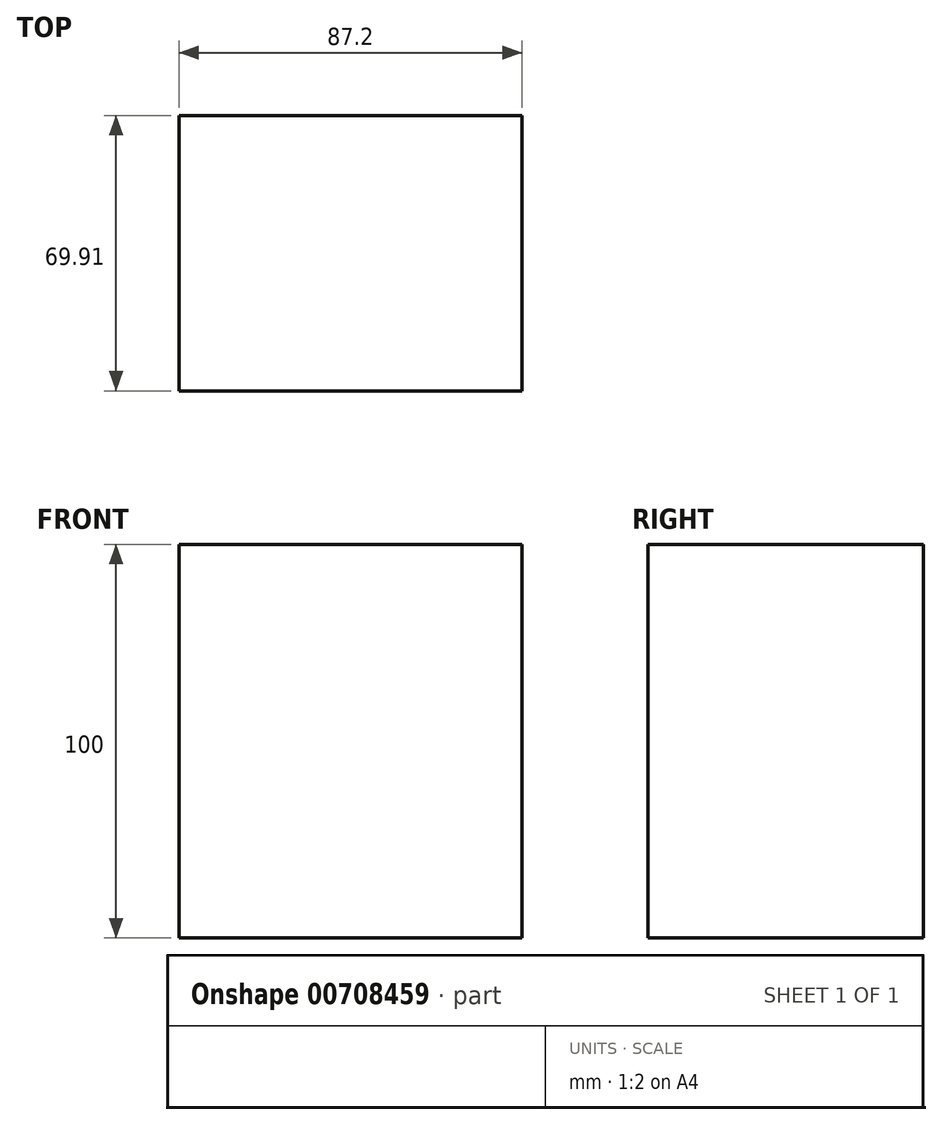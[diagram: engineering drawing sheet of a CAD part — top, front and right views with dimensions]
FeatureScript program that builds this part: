
annotation { "Feature Type Name" : "Feature", "Feature Type Description" : "" }
export const myFeature = defineFeature(function(context is Context, id is Id, definition is map)
    precondition{}
    {
        {
            var Q0;
            Q0=qCreatedBy(makeId("Top.planeOp"),FACE);
            var sketch = newSketch(context, id + "F0", { "sketchPlane" : qUnion([Q0])});
            skLineSegment(sketch, "E0.bottom", {"start": v(-123.08, -57.25) * mm, "end": v(-35.88, -57.25) * mm});
            skLineSegment(sketch, "E0.top", {"start": v(-123.08, 12.66) * mm, "end": v(-35.88, 12.66) * mm});
            skLineSegment(sketch, "E0.left", {"start": v(-123.08, -57.25) * mm, "end": v(-123.08, 12.66) * mm});
            skLineSegment(sketch, "E0.right", {"start": v(-35.88, -57.25) * mm, "end": v(-35.88, 12.66) * mm});
            skLineSegment(sketch, "E1.bottom", {"start": v(-4.7, -32.25) * mm, "end": v(64.7, -32.25) * mm});
            skLineSegment(sketch, "E1.top", {"start": v(-4.7, 35.78) * mm, "end": v(64.7, 35.78) * mm});
            skLineSegment(sketch, "E1.left", {"start": v(-4.7, -32.25) * mm, "end": v(-4.7, 35.78) * mm});
            skLineSegment(sketch, "E1.right", {"start": v(64.7, -32.25) * mm, "end": v(64.7, 35.78) * mm});
            skSolve(sketch);
        }
        {
            assignVariable(context, id + "F1", {"name" : "lenght", "anyValue" : 100});
        }
        {
            var Q0;
            Q0=makeQuery(id+"F0.imprint","IMPRINT",FACE,{"disambiguationData":[TD([[makeQuery(id+"F0.imprint","IMPRINT",EDGE,{"derivedFrom":sQuery(id+"F0.wireOp",EDGE,"E0.bottom")}),1.0]])]});
            extrude(context, id + "F2", {"entities" : qUnion([Q0]), "depth" : (getVariable(context, 'lenght')) * mm, "offsetDistance" : 25 * mm});
        }
    });
